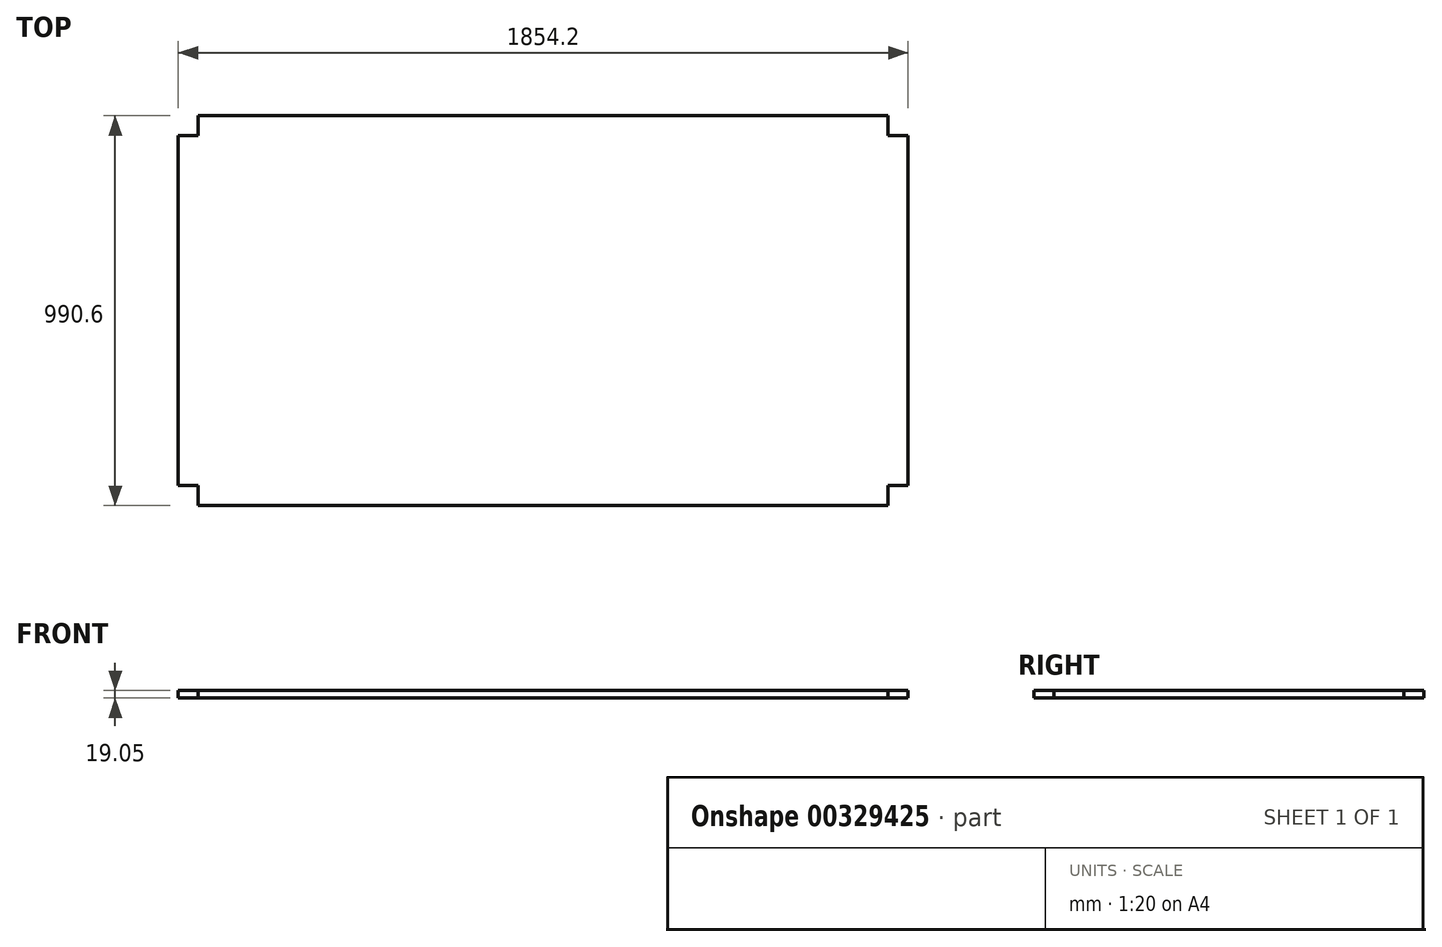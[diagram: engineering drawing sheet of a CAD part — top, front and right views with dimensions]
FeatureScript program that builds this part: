
annotation { "Feature Type Name" : "Feature", "Feature Type Description" : "" }
export const myFeature = defineFeature(function(context is Context, id is Id, definition is map)
    precondition{}
    {
        {
            var Q0;
            Q0=qCreatedBy(makeId("Top.planeOp"),FACE);
            var sketch = newSketch(context, id + "F0", { "sketchPlane" : qUnion([Q0])});
            skLineSegment(sketch, "E0.bottom", {"start": v(876.3, -495.3) * mm, "end": v(-876.3, -495.3) * mm});
            skLineSegment(sketch, "E0.top", {"start": v(876.3, 495.3) * mm, "end": v(-876.3, 495.3) * mm});
            skLineSegment(sketch, "E0.left", {"start": v(927.1, -444.5) * mm, "end": v(927.1, 444.5) * mm});
            skLineSegment(sketch, "E0.right", {"start": v(-927.1, -444.5) * mm, "end": v(-927.1, 444.5) * mm});
            skPoint(sketch, "E0.middle", {"position": v(0, 0) * mm});
            skLineSegment(sketch, "E1.top", {"start": v(-927.1, 444.5) * mm, "end": v(-876.3, 444.5) * mm});
            skLineSegment(sketch, "E1.right", {"start": v(-876.3, 495.3) * mm, "end": v(-876.3, 444.5) * mm});
            skPoint(sketch, "E2.orphan", {"position": v(-927.1, 495.3) * mm});
            skLineSegment(sketch, "E3.MirrorCS", {"start": v(876.3, 495.3) * mm, "end": v(876.3, 444.5) * mm});
            skLineSegment(sketch, "E4.MirrorCS", {"start": v(927.1, 444.5) * mm, "end": v(876.3, 444.5) * mm});
            skPoint(sketch, "E5.MirrorP", {"position": v(927.1, 495.3) * mm});
            skLineSegment(sketch, "E6.MirrorCS", {"start": v(-876.3, -495.3) * mm, "end": v(-876.3, -444.5) * mm});
            skLineSegment(sketch, "E7.MirrorCS", {"start": v(-927.1, -444.5) * mm, "end": v(-876.3, -444.5) * mm});
            skPoint(sketch, "E8.MirrorP", {"position": v(-927.1, -495.3) * mm});
            skLineSegment(sketch, "E9.MirrorCS", {"start": v(927.1, -444.5) * mm, "end": v(876.3, -444.5) * mm});
            skLineSegment(sketch, "E10.MirrorCS", {"start": v(876.3, -495.3) * mm, "end": v(876.3, -444.5) * mm});
            skPoint(sketch, "E11.MirrorP", {"position": v(927.1, -495.3) * mm});
            skSolve(sketch);
        }
        {
            var Q0;
            Q0=qSketchRegion(id+"F0",true);
            extrude(context, id + "F1", {"entities" : qUnion([Q0]), "depth" : 19.05 * mm});
        }
    });
